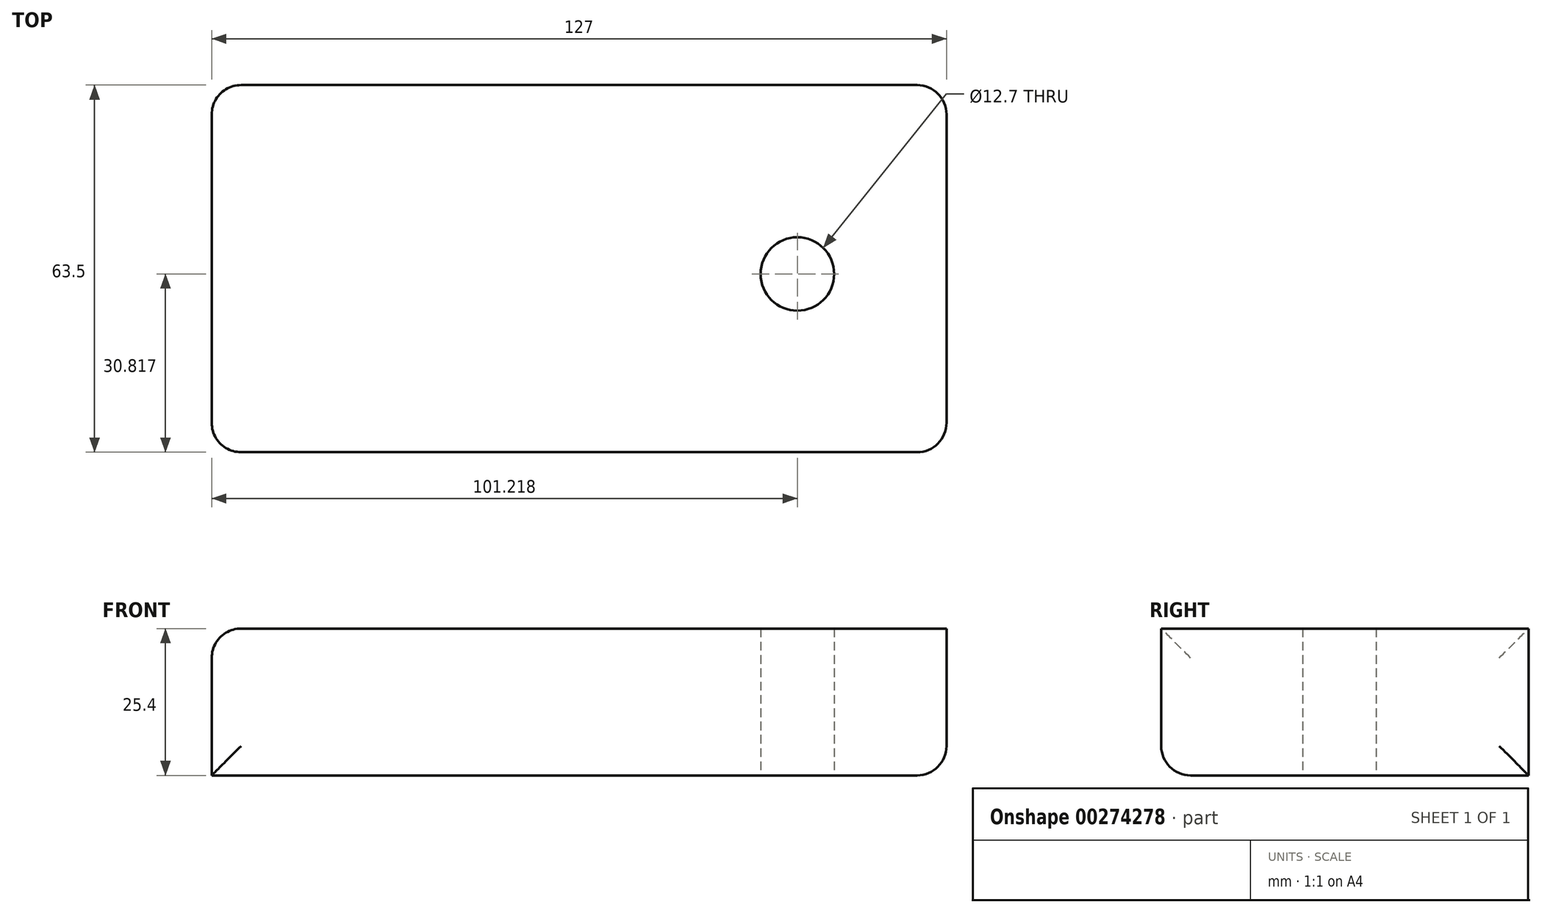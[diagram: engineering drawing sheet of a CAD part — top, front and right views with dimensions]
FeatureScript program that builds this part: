
annotation { "Feature Type Name" : "Feature", "Feature Type Description" : "" }
export const myFeature = defineFeature(function(context is Context, id is Id, definition is map)
    precondition{}
    {
        {
            var Q0;
            Q0=qCreatedBy(makeId("Top.planeOp"),FACE);
            var sketch = newSketch(context, id + "F0", { "sketchPlane" : qUnion([Q0])});
            skLineSegment(sketch, "E0.bottom", {"start": v(0, 0) * mm, "end": v(127, 0) * mm});
            skLineSegment(sketch, "E0.top", {"start": v(0, 63.5) * mm, "end": v(127, 63.5) * mm});
            skLineSegment(sketch, "E0.left", {"start": v(0, 0) * mm, "end": v(0, 63.5) * mm});
            skLineSegment(sketch, "E0.right", {"start": v(127, 0) * mm, "end": v(127, 63.5) * mm});
            skSolve(sketch);
        }
        {
            var Q0;
            Q0=makeQuery(id+"F0.imprint","IMPRINT",FACE,{"disambiguationData":[TD([[makeQuery(id+"F0.imprint","IMPRINT",EDGE,{"derivedFrom":sQuery(id+"F0.wireOp",EDGE,"E0.bottom")}),1.0]])]});
            extrude(context, id + "F1", {"entities" : qUnion([Q0]), "depth" : 25.4 * mm});
        }
        {
            var Q0;
            Q0=makeQuery(id+"F1.opExtrude","CAP_FACE",FACE,{"disambiguationData":[OSD([sQuery(id+"F0.wireOp",EDGE,"E0.bottom"),sQuery(id+"F0.wireOp",EDGE,"E0.top"),sQuery(id+"F0.wireOp",EDGE,"E0.left"),sQuery(id+"F0.wireOp",EDGE,"E0.right")])],"isStart":true});
            var sketch = newSketch(context, id + "F2", { "sketchPlane" : qUnion([Q0])});
            skCircle(sketch, "E1", {"center": v(101.22, -30.82) * mm, "radius": 10.64 * mm});
            skSolve(sketch);
        }
        {
            var Q0;
            Q0=sQuery(id+"F2.wireOp",VERTEX,"E1.center");
            var Q1;
            Q1=makeQuery(id+"F1.opExtrude","SWEPT_BODY",BODY,{"disambiguationData":[OSD([sQuery(id+"F0.wireOp",EDGE,"E0.bottom"),sQuery(id+"F0.wireOp",EDGE,"E0.top"),sQuery(id+"F0.wireOp",EDGE,"E0.left"),sQuery(id+"F0.wireOp",EDGE,"E0.right")])]});
            hole(context, id + "F3", {"style" : HoleStyle.C_BORE, "endStyle" : HoleEndStyle.THROUGH, "holeDiameter" : 12.7 * mm, "cBoreDiameter" : 12.7 * mm, "cBoreDepth" : 6.35 * mm, "tappedDepth" : 12.7 * mm, "tapClearance" : 3, "locations" : qUnion([Q0]), "scope" : qUnion([Q1])});
        }
        {
            var Q0;
            Q0=makeQuery(id+"F1.opExtrude","CAP_EDGE",EDGE,{"disambiguationData":[OSD([sQuery(id+"F0.wireOp",EDGE,"E0.right")])],"isStart":true});
            var Q1;
            Q1=makeQuery(id+"F1.opExtrude","SWEPT_EDGE",EDGE,{"disambiguationData":[OSD([sQuery(id+"F0.wireOp",EDGE,"E0.top"),sQuery(id+"F0.wireOp",EDGE,"E0.right")])]});
            var Q2;
            Q2=makeQuery(id+"F1.opExtrude","SWEPT_EDGE",EDGE,{"disambiguationData":[OSD([sQuery(id+"F0.wireOp",EDGE,"E0.bottom"),sQuery(id+"F0.wireOp",EDGE,"E0.right")])]});
            var Q3;
            Q3=makeQuery(id+"F1.opExtrude","CAP_EDGE",EDGE,{"disambiguationData":[OSD([sQuery(id+"F0.wireOp",EDGE,"E0.bottom")])],"isStart":true});
            var Q4;
            Q4=makeQuery(id+"F1.opExtrude","SWEPT_EDGE",EDGE,{"disambiguationData":[OSD([sQuery(id+"F0.wireOp",EDGE,"E0.bottom"),sQuery(id+"F0.wireOp",EDGE,"E0.left")])]});
            var Q5;
            Q5=makeQuery(id+"F1.opExtrude","CAP_EDGE",EDGE,{"disambiguationData":[OSD([sQuery(id+"F0.wireOp",EDGE,"E0.left")])],"isStart":false});
            var Q6;
            Q6=makeQuery(id+"F1.opExtrude","SWEPT_EDGE",EDGE,{"disambiguationData":[OSD([sQuery(id+"F0.wireOp",EDGE,"E0.top"),sQuery(id+"F0.wireOp",EDGE,"E0.left")])]});
            fillet(context, id + "F4", {"entities" : qUnion([Q0, Q1, Q2, Q3, Q4, Q5, Q6]), "radius" : 5.08 * mm, "tangentPropagation" : true, "allowEdgeOverflow" : false});
        }
    });
